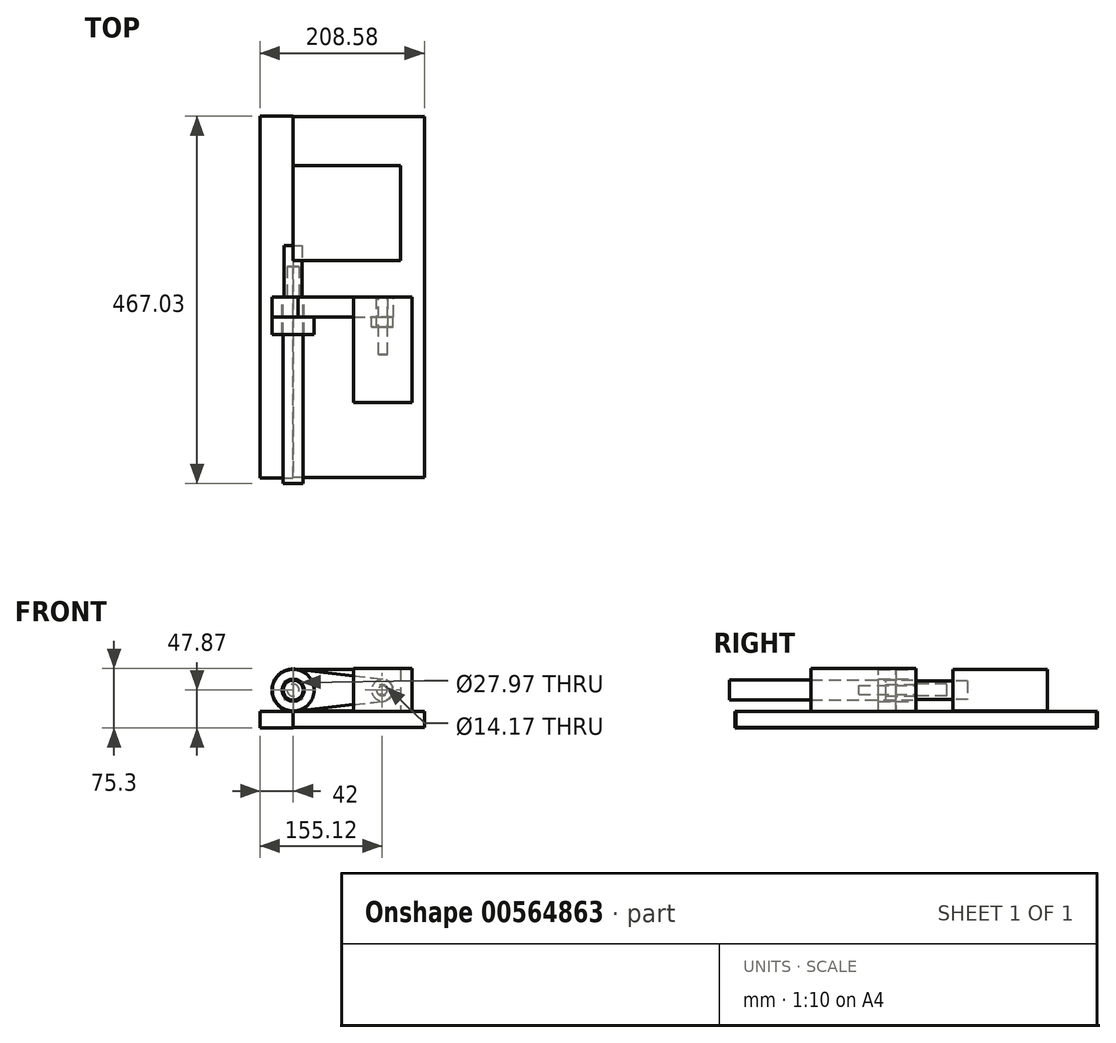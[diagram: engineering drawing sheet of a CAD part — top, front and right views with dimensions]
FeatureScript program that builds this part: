
annotation { "Feature Type Name" : "Feature", "Feature Type Description" : "" }
export const myFeature = defineFeature(function(context is Context, id is Id, definition is map)
    precondition{}
    {
        {
            var Q0;
            Q0=qCreatedBy(makeId("Front.planeOp"),FACE);
            var sketch = newSketch(context, id + "F0", { "sketchPlane" : qUnion([Q0])});
            skCircle(sketch, "E0", {"center": v(0, 0) * mm, "radius": 26.9 * mm});
            skCircle(sketch, "E1", {"center": v(0, 0) * mm, "radius": 14.33 * mm});
            skCircle(sketch, "E2", {"center": v(113.13, 0) * mm, "radius": 14.12 * mm});
            skCircle(sketch, "E3", {"center": v(113.13, 0) * mm, "radius": 8.1 * mm});
            skLineSegment(sketch, "E4", {"start": v(0, 26.9) * mm, "end": v(114.7, 14.03) * mm});
            skLineSegment(sketch, "E5", {"start": v(114.7, 14.03) * mm, "end": v(114.7, 14.03) * mm});
            skLineSegment(sketch, "E6", {"start": v(113.13, 0) * mm, "end": v(113.13, 0) * mm});
            skLineSegment(sketch, "E7", {"start": v(108.87, -34.56) * mm, "end": v(121.64, -46.13) * mm});
            skLineSegment(sketch, "E8", {"start": v(121.64, -46.13) * mm, "end": v(111.97, -19.48) * mm});
            skLineSegment(sketch, "E9", {"start": v(111.97, -19.48) * mm, "end": v(119.47, -40.14) * mm});
            skLineSegment(sketch, "E10", {"start": v(0, -26.9) * mm, "end": v(114.7, -14.03) * mm});
            skLineSegment(sketch, "E11", {"start": v(114.7, -14.03) * mm, "end": v(119.47, -40.14) * mm});
            skSolve(sketch);
        }
        {
            var Q0;
            Q0 = qSketchRegion(id + "F0", true);
            extrude(context, id + "F1", {"entities" : qUnion([Q0]), "depth" : 25.45 * mm, "offsetDistance" : 25.4 * mm});
        }
        {
            var Q0;
            Q0=qCreatedBy(makeId("Front.planeOp"),FACE);
            var sketch = newSketch(context, id + "F2", { "sketchPlane" : qUnion([Q0])});
            skCircle(sketch, "E12", {"center": v(0, 0) * mm, "radius": 26.47 * mm});
            skCircle(sketch, "E13", {"center": v(0, 0) * mm, "radius": 13.99 * mm});
            skSolve(sketch);
        }
        {
            var Q0;
            Q0=makeQuery(id+"F2.imprint","IMPRINT",FACE,{"disambiguationData":[TD([[makeQuery(id+"F2.imprint","IMPRINT",EDGE,{"derivedFrom":sQuery(id+"F2.wireOp",EDGE,"E12")}),1.0]])]});
            extrude(context, id + "F3", {"entities" : qUnion([Q0]), "operationType" : NewBodyOperationType.ADD, "depth" : 47.63 * mm, "offsetDistance" : 25.4 * mm});
        }
        {
            var Q0;
            Q0=qCreatedBy(makeId("Front.planeOp"),FACE);
            var sketch = newSketch(context, id + "F4", { "sketchPlane" : qUnion([Q0])});
            skCircle(sketch, "E14", {"center": v(113.12, 0) * mm, "radius": 13.47 * mm});
            skCircle(sketch, "E15", {"center": v(113.12, 0) * mm, "radius": 7.08 * mm});
            skSolve(sketch);
        }
        {
            var Q0;
            Q0=makeQuery(id+"F4.imprint","IMPRINT",FACE,{"disambiguationData":[TD([[makeQuery(id+"F4.imprint","IMPRINT",EDGE,{"derivedFrom":sQuery(id+"F4.wireOp",EDGE,"E14")}),1.0]])]});
            extrude(context, id + "F5", {"entities" : qUnion([Q0]), "operationType" : NewBodyOperationType.ADD, "depth" : 38.4 * mm, "offsetDistance" : 25.4 * mm});
        }
        {
            var Q0;
            Q0=qCreatedBy(makeId("Front.planeOp"),FACE);
            var sketch = newSketch(context, id + "F6", { "sketchPlane" : qUnion([Q0])});
            skCircle(sketch, "E16", {"center": v(0, 0) * mm, "radius": 12.7 * mm});
            skSolve(sketch);
        }
        {
            var Q0;
            Q0=makeQuery(id+"F6.imprint","IMPRINT",FACE,{"disambiguationData":[TD([[makeQuery(id+"F6.imprint","IMPRINT",EDGE,{"derivedFrom":sQuery(id+"F6.wireOp",EDGE,"E16")}),1.0]])]});
            extrude(context, id + "F7", {"entities" : qUnion([Q0]), "depth" : 236.97 * mm, "offsetDistance" : 25.4 * mm});
        }
        {
            var Q0;
            Q0=qCreatedBy(makeId("Front.planeOp"),FACE);
            var sketch = newSketch(context, id + "F8", { "sketchPlane" : qUnion([Q0])});
            skCircle(sketch, "E17", {"center": v(0, 0) * mm, "radius": 7.63 * mm});
            skSolve(sketch);
        }
        {
            var Q0;
            Q0=makeQuery(id+"F8.imprint","IMPRINT",FACE,{"disambiguationData":[TD([[makeQuery(id+"F8.imprint","IMPRINT",EDGE,{"derivedFrom":sQuery(id+"F8.wireOp",EDGE,"E17")}),1.0]])]});
            extrude(context, id + "F9", {"entities" : qUnion([Q0]), "operationType" : NewBodyOperationType.ADD, "oppositeDirection" : true, "depth" : 38.98 * mm, "offsetDistance" : 25.4 * mm});
        }
        {
            var Q0;
            Q0=qCreatedBy(makeId("Right.planeOp"),FACE);
            var sketch = newSketch(context, id + "F10", { "sketchPlane" : qUnion([Q0])});
            skLineSegment(sketch, "E18.bottom", {"start": v(228.97, -27.13) * mm, "end": v(-228.97, -27.13) * mm});
            skLineSegment(sketch, "E18.top", {"start": v(228.97, -47.11) * mm, "end": v(-228.97, -47.11) * mm});
            skLineSegment(sketch, "E18.left", {"start": v(228.97, -27.13) * mm, "end": v(228.97, -47.11) * mm});
            skLineSegment(sketch, "E18.right", {"start": v(-228.97, -27.13) * mm, "end": v(-228.97, -47.11) * mm});
            skPoint(sketch, "E18.middle", {"position": v(0, -37.12) * mm});
            skSolve(sketch);
        }
        {
            var Q0;
            Q0=makeQuery(id+"F10.imprint","IMPRINT",FACE,{"disambiguationData":[TD([[makeQuery(id+"F10.imprint","IMPRINT",EDGE,{"derivedFrom":sQuery(id+"F10.wireOp",EDGE,"E18.bottom")}),1.0]])]});
            extrude(context, id + "F11", {"entities" : qUnion([Q0]), "depth" : 166.58 * mm, "offsetDistance" : 25.4 * mm});
        }
        {
            var Q0;
            Q0=qCreatedBy(makeId("Front.planeOp"),FACE);
            var sketch = newSketch(context, id + "F12", { "sketchPlane" : qUnion([Q0])});
            skCircle(sketch, "E19", {"center": v(113.76, 0) * mm, "radius": 5.81 * mm});
            skSolve(sketch);
        }
        {
            var Q0;
            Q0=sQuery(id+"F12.wireOp",EDGE,"E19");
            extrude(context, id + "F13", {"bodyType" : ToolBodyType.SURFACE, "surfaceEntities" : qUnion([Q0]), "oppositeDirection" : true, "depth" : 48.12 * mm, "offsetDistance" : 25.4 * mm});
        }
        {
            var Q0;
            Q0=qCreatedBy(makeId("Right.planeOp"),FACE);
            var sketch = newSketch(context, id + "F14", { "sketchPlane" : qUnion([Q0])});
            skLineSegment(sketch, "E20.bottom", {"start": v(166.9, 26.36) * mm, "end": v(46.57, 26.36) * mm});
            skLineSegment(sketch, "E20.top", {"start": v(166.9, -26.36) * mm, "end": v(46.57, -26.36) * mm});
            skLineSegment(sketch, "E20.left", {"start": v(166.9, 26.36) * mm, "end": v(166.9, -26.36) * mm});
            skLineSegment(sketch, "E20.right", {"start": v(46.57, 26.36) * mm, "end": v(46.57, -26.36) * mm});
            skPoint(sketch, "E20.middle", {"position": v(106.73, 0) * mm});
            skSolve(sketch);
        }
        {
            var Q0;
            Q0=makeQuery(id+"F14.imprint","IMPRINT",FACE,{"disambiguationData":[TD([[makeQuery(id+"F14.imprint","IMPRINT",EDGE,{"derivedFrom":sQuery(id+"F14.wireOp",EDGE,"E20.bottom")}),1.0]])]});
            extrude(context, id + "F15", {"entities" : qUnion([Q0]), "depth" : 136.1 * mm, "offsetDistance" : 25.4 * mm});
        }
        {
            var Q0;
            Q0=qCreatedBy(makeId("Right.planeOp"),FACE);
            var sketch = newSketch(context, id + "F16", { "sketchPlane" : qUnion([Q0])});
            skLineSegment(sketch, "E21.bottom", {"start": v(-230.06, -26.95) * mm, "end": v(230.06, -26.95) * mm});
            skLineSegment(sketch, "E21.top", {"start": v(-230.06, -47.87) * mm, "end": v(230.06, -47.87) * mm});
            skLineSegment(sketch, "E21.left", {"start": v(-230.06, -26.95) * mm, "end": v(-230.06, -47.87) * mm});
            skLineSegment(sketch, "E21.right", {"start": v(230.06, -26.95) * mm, "end": v(230.06, -47.87) * mm});
            skPoint(sketch, "E21.middle", {"position": v(0, -37.41) * mm});
            skSolve(sketch);
        }
        {
            var Q0;
            Q0=makeQuery(id+"F16.imprint","IMPRINT",FACE,{"disambiguationData":[TD([[makeQuery(id+"F16.imprint","IMPRINT",EDGE,{"derivedFrom":sQuery(id+"F16.wireOp",EDGE,"E21.bottom")}),-1.0]])]});
            extrude(context, id + "F17", {"entities" : qUnion([Q0]), "operationType" : NewBodyOperationType.ADD, "oppositeDirection" : true, "depth" : 42 * mm, "offsetDistance" : 25.4 * mm});
        }
        {
            var Q0;
            Q0=qCreatedBy(makeId("Front.planeOp"),FACE);
            var sketch = newSketch(context, id + "F18", { "sketchPlane" : qUnion([Q0])});
            skLineSegment(sketch, "E22.bottom", {"start": v(-11.46, 11.56) * mm, "end": v(11.46, 11.56) * mm});
            skLineSegment(sketch, "E22.top", {"start": v(-11.46, -11.56) * mm, "end": v(11.46, -11.56) * mm});
            skLineSegment(sketch, "E22.left", {"start": v(-11.46, 11.56) * mm, "end": v(-11.46, -11.56) * mm});
            skLineSegment(sketch, "E22.right", {"start": v(11.46, 11.56) * mm, "end": v(11.46, -11.56) * mm});
            skPoint(sketch, "E22.middle", {"position": v(0, 0) * mm});
            skSolve(sketch);
        }
        {
            var Q0;
            Q0=makeQuery(id+"F18.imprint","IMPRINT",FACE,{"disambiguationData":[TD([[makeQuery(id+"F18.imprint","IMPRINT",EDGE,{"derivedFrom":sQuery(id+"F18.wireOp",EDGE,"E22.bottom")}),-1.0]])]});
            extrude(context, id + "F19", {"entities" : qUnion([Q0]), "oppositeDirection" : true, "depth" : 65.3 * mm, "offsetDistance" : 25.4 * mm});
        }
        {
            var Q0;
            Q0=qCreatedBy(makeId("Front.planeOp"),FACE);
            var sketch = newSketch(context, id + "F20", { "sketchPlane" : qUnion([Q0])});
            skCircle(sketch, "E23", {"center": v(0, 0) * mm, "radius": 7.72 * mm});
            skLineSegment(sketch, "E24", {"start": v(-7.72, 0) * mm, "end": v(-56.44, -27.14) * mm});
            skLineSegment(sketch, "E25", {"start": v(-56.44, -27.14) * mm, "end": v(-56.44, -27.14) * mm});
            skLineSegment(sketch, "E26", {"start": v(-56.44, -27.14) * mm, "end": v(-52.13, -34.88) * mm});
            skLineSegment(sketch, "E27", {"start": v(-52.13, -34.88) * mm, "end": v(0, -7.72) * mm});
            skLineSegment(sketch, "E28", {"start": v(0, -7.72) * mm, "end": v(-52.13, -34.88) * mm});
            skSolve(sketch);
        }
        {
            var Q0;
            Q0=sQuery(id+"F20.wireOp",EDGE,"E23");
            extrude(context, id + "F21", {"bodyType" : ToolBodyType.SURFACE, "surfaceEntities" : qUnion([Q0]), "depth" : 291.58 * mm, "offsetDistance" : 25.4 * mm});
        }
        {
            var Q0;
            Q0=qCreatedBy(makeId("Front.planeOp"),FACE);
            var sketch = newSketch(context, id + "F22", { "sketchPlane" : qUnion([Q0])});
            skCircle(sketch, "E29", {"center": v(113.86, 0) * mm, "radius": 5.71 * mm});
            skSolve(sketch);
        }
        {
            var Q0;
            Q0=makeQuery(id+"F22.imprint","IMPRINT",FACE,{"disambiguationData":[TD([[makeQuery(id+"F22.imprint","IMPRINT",EDGE,{"derivedFrom":sQuery(id+"F22.wireOp",EDGE,"E29")}),1.0]])]});
            extrude(context, id + "F23", {"entities" : qUnion([Q0]), "depth" : 72.87 * mm, "offsetDistance" : 25.4 * mm});
        }
        {
            var Q0;
            Q0=qCreatedBy(makeId("Front.planeOp"),FACE);
            var sketch = newSketch(context, id + "F24", { "sketchPlane" : qUnion([Q0])});
            skLineSegment(sketch, "E30.bottom", {"start": v(151.25, 27.43) * mm, "end": v(76.38, 27.43) * mm});
            skLineSegment(sketch, "E30.top", {"start": v(151.25, -27.43) * mm, "end": v(76.38, -27.43) * mm});
            skLineSegment(sketch, "E30.left", {"start": v(151.25, 27.43) * mm, "end": v(151.25, -27.43) * mm});
            skLineSegment(sketch, "E30.right", {"start": v(76.38, 27.43) * mm, "end": v(76.38, -27.43) * mm});
            skPoint(sketch, "E30.middle", {"position": v(113.82, 0) * mm});
            skSolve(sketch);
        }
        {
            var Q0;
            Q0=makeQuery(id+"F24.imprint","IMPRINT",FACE,{"disambiguationData":[TD([[makeQuery(id+"F24.imprint","IMPRINT",EDGE,{"derivedFrom":sQuery(id+"F24.wireOp",EDGE,"E30.bottom")}),1.0]])]});
            extrude(context, id + "F25", {"entities" : qUnion([Q0]), "depth" : 133.8 * mm, "offsetDistance" : 25.4 * mm});
        }
        {
            var Q0;
            Q0=qCreatedBy(makeId("Top.planeOp"),FACE);
            var sketch = newSketch(context, id + "F26", { "sketchPlane" : qUnion([Q0])});
            skLineSegment(sketch, "E31", {"start": v(162.98, -227.77) * mm, "end": v(162.98, 226.97) * mm});
            skLineSegment(sketch, "E32", {"start": v(162.98, 226.97) * mm, "end": v(162.98, -227.77) * mm});
            skLineSegment(sketch, "E33", {"start": v(-44.26, -227.77) * mm, "end": v(-44.26, 229.42) * mm});
            skSolve(sketch);
        }
        {
            var Q0;
            Q0=sQuery(id+"F26.wireOp",EDGE,"E32");
            extrude(context, id + "F27", {"bodyType" : ToolBodyType.SURFACE, "surfaceEntities" : qUnion([Q0]), "depth" : 55.82 * mm, "offsetDistance" : 25.4 * mm});
        }
        {
            var Q0;
            Q0=makeQuery(id+"F27.opExtrude","SWEPT_BODY",BODY,{"disambiguationData":[OSD([sQuery(id+"F26.wireOp",EDGE,"E32")])]});
            deleteBodies(context, id + "F28", {"entities" : qUnion([Q0])});
        }
    });
